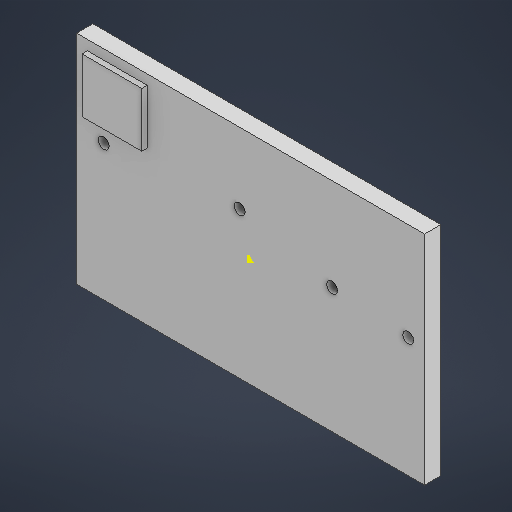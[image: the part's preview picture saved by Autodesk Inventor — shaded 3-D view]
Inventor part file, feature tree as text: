
AUTODESK INVENTOR PART (.ipt)
format: ipt  version: 2025 (Build 290162000, 162)  size: 202,752 bytes
history: native  units: mm
features: sketch x4, extrude x3
ambient origin geometry x8: Origin, YZ Plane, XZ Plane, XY Plane, X Axis, Y Axis, Z Axis, Center Point
bodies: 实体1 (feature_tree)
feature tree (7):
  extrude  "拉伸1"  Depth=40.0mm
  extrude  "拉伸2"  Depth=2.0mm
  extrude  "拉伸3"  Depth=2.0mm
  sketch  "草图5"  dims[d11=5.0mm d12=15.0mm d13=2.0mm d14=25.0mm d16=2.0mm d17=2.0mm d19=4.0mm d20=17.0mm d21=2.0mm d22=1.0mm d23=3.0mm d24=14.0mm d25=10.0mm d26=0.0mm d27=2.0mm d28=10.0mm d29=11.0mm d30=1.0mm d31=0.0mm]
  sketch  "草图1"  dims[d0=64.0mm d1=40.0mm]
  sketch  "草图3"  dims[d2=2.0mm d3=30.0mm]
  sketch  "草图4"  dims[d4=3.0mm d5=0.0mm d10=2.0mm]
